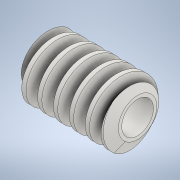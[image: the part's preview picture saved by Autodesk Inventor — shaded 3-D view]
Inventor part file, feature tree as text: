
AUTODESK INVENTOR PART (.ipt)
format: ipt  version: 2022.2 (Build 262287010, 287A)  size: 332,288 bytes
history: native  units: mm (DEFAULTED — no unit token found)
features: other x6, extrude x2, chamfer x2, pattern_circular x2, sketch x2, plane x1
ambient origin geometry x6: Origin, XZ Plane, X Axis, Y Axis, Z Axis, Center Point
bodies: Solid1 (feature_tree)
feature tree (15):
  extrude  "Base Body"  Depth=24.255213mm
  chamfer  "Chamfer1"  [1 undecoded]
  chamfer  "Chamfer2"  Distance=1.618499mm
  other  "Tooth Sketch"
  other  "Left Tooth"
  pattern_circular  "Left Tooth Pattern"  [2 undecoded]
  other  "Tooth"
  pattern_circular  "Tooth Pattern"  [2 undecoded]
  plane  "Work Plane10"
  extrude  "Extrusion2"  Depth=10.0mm
  other  "Base Body Sketch"
  sketch  "Sketch5"  dims[d4=40.0mm d5=24.255213mm]
  other  "Srf1"
  sketch  "Sketch6"  dims[d6=38.1mm d7=0.0mm d8=1.618499mm d9=4.446789mm d10=1.618499mm d11=4.446789mm d12=19.198622mm d14=3.1425mm d24=19.198622mm d25=28.575mm d26=1.5875mm d27=7.680818mm d28=10.106339mm d29=12.248883mm d30=6.35mm d31=10.0mm d32=90.0mm d33=0.0mm d34=90.0deg d35=90.0deg d36=0.0mm d37=0.0mm d43=10.0mm d45=360.0deg d46=45.0deg d47=45.0deg d49=0.0mm d53=0.0mm d54=70.744372mm d55=0.0mm d56=0.0mm d57=20.212678mm d58=25.4mm d59=0.0mm d60=6.35mm d61=25.4mm d62=90.0mm d63=0.0mm d64=90.0deg d65=90.0deg d66=0.0mm d67=0.0mm d68=10.0mm d69=10.0mm d70=360.0deg d72=10.0mm d74=10.0mm d75=10.0mm d76=0.0mm d77=70.744372mm d78=9.525mm d79=0.0mm d80=0.0mm d81=12.7mm]
  other  "Pitch Diameter"
note: 5 required parameter values undecoded (feature->parameter linkage not recoverable at this tier; creation-order binding heuristic only, values carry confidence <= 0.55)
